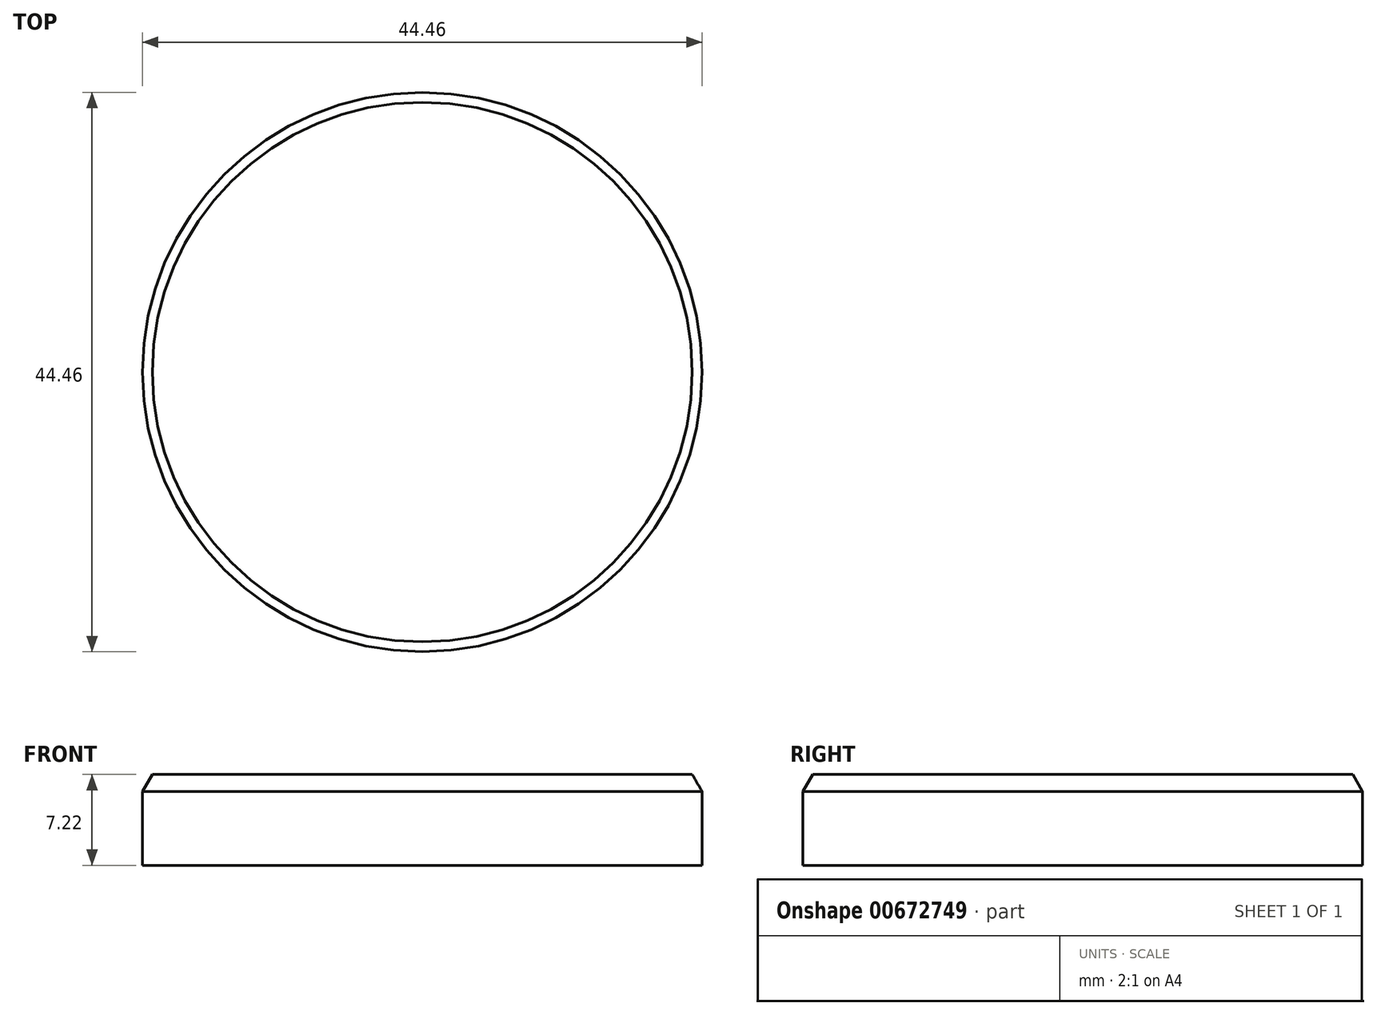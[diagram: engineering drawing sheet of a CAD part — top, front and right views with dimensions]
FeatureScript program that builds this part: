
annotation { "Feature Type Name" : "Feature", "Feature Type Description" : "" }
export const myFeature = defineFeature(function(context is Context, id is Id, definition is map)
    precondition{}
    {
        {
            var Q0;
            Q0=qCreatedBy(makeId("Top.planeOp"),FACE);
            var sketch = newSketch(context, id + "F0", { "sketchPlane" : qUnion([Q0])});
            skCircle(sketch, "E0", {"center": v(0, 0) * mm, "radius": 22.23 * mm});
            skSolve(sketch);
        }
        {
            var Q0;
            Q0 = qSketchRegion(id + "F0", true);
            extrude(context, id + "F1", {"entities" : qUnion([Q0]), "depth" : 7.2 * mm, "offsetDistance" : 25 * mm});
        }
        {
            var Q0;
            Q0=makeQuery(id+"F1.opExtrude","CAP_FACE",FACE,{"disambiguationData":[OSD([sQuery(id+"F0.wireOp",EDGE,"E0")])],"isStart":false});
            var sketch = newSketch(context, id + "F2", { "sketchPlane" : qUnion([Q0])});
            skSolve(sketch);
        }
        {
            var Q0;
            Q0=makeQuery(id+"F1.opExtrude","CAP_EDGE",EDGE,{"disambiguationData":[OSD([sQuery(id+"F0.wireOp",EDGE,"E0")])],"isStart":false});
            chamfer(context, id + "F3", {"entities" : qUnion([Q0]), "chamferType" : ChamferType.OFFSET_ANGLE, "width" : 1.36 * mm, "oppositeDirection" : true, "angle" : 30 * degree, "tangentPropagation" : true});
        }
    });
